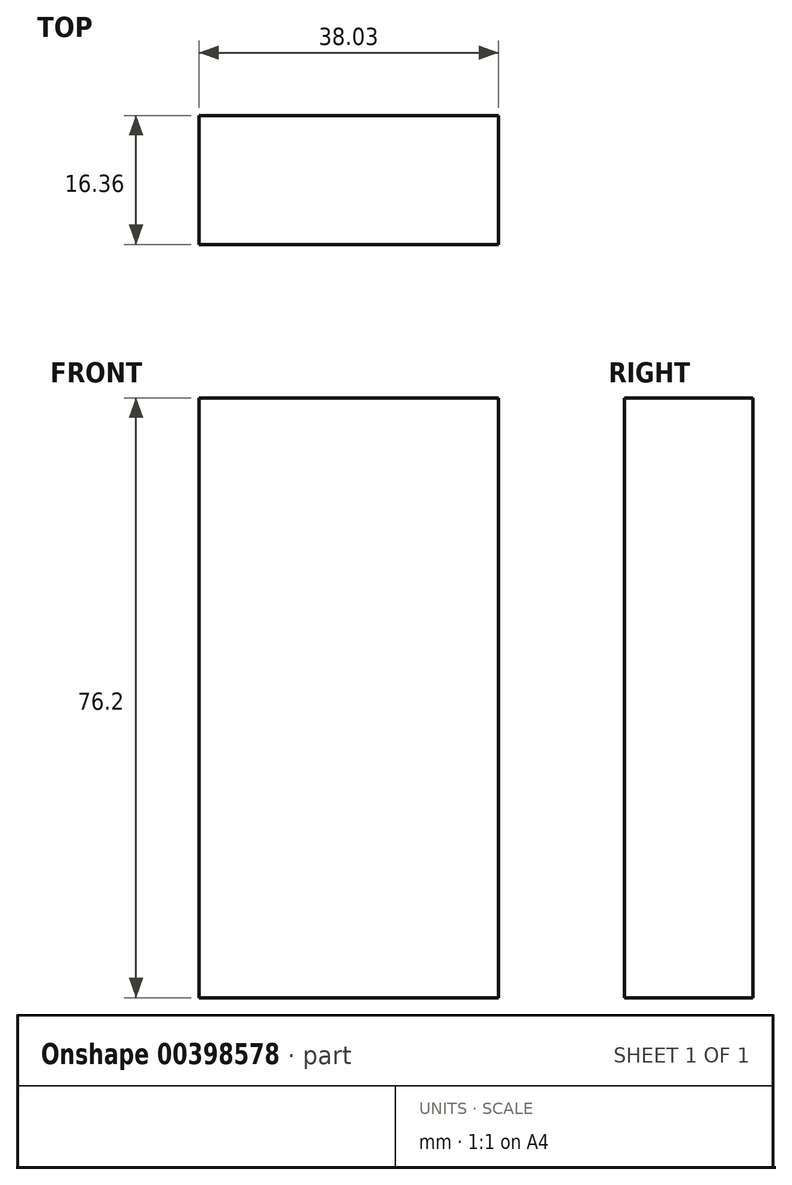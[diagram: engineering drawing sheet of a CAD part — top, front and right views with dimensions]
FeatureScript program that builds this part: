
annotation { "Feature Type Name" : "Feature", "Feature Type Description" : "" }
export const myFeature = defineFeature(function(context is Context, id is Id, definition is map)
    precondition{}
    {
        {
            var Q0;
            Q0=qCreatedBy(makeId("Top.planeOp"),FACE);
            var sketch = newSketch(context, id + "F0", { "sketchPlane" : qUnion([Q0])});
            skLineSegment(sketch, "E0.bottom", {"start": v(-52.42, 29.17) * mm, "end": v(-14.39, 29.17) * mm});
            skLineSegment(sketch, "E0.top", {"start": v(-52.42, 12.8) * mm, "end": v(-14.39, 12.8) * mm});
            skLineSegment(sketch, "E0.left", {"start": v(-52.42, 29.17) * mm, "end": v(-52.42, 12.8) * mm});
            skLineSegment(sketch, "E0.right", {"start": v(-14.39, 29.17) * mm, "end": v(-14.39, 12.8) * mm});
            skSolve(sketch);
        }
        {
            var Q0;
            Q0=makeQuery(id+"F0.imprint","IMPRINT",FACE,{"disambiguationData":[TD([[makeQuery(id+"F0.imprint","IMPRINT",EDGE,{"derivedFrom":sQuery(id+"F0.wireOp",EDGE,"E0.bottom")}),-1.0]])]});
            extrude(context, id + "F1", {"entities" : qUnion([Q0]), "depth" : 76.2 * mm});
        }
    });
